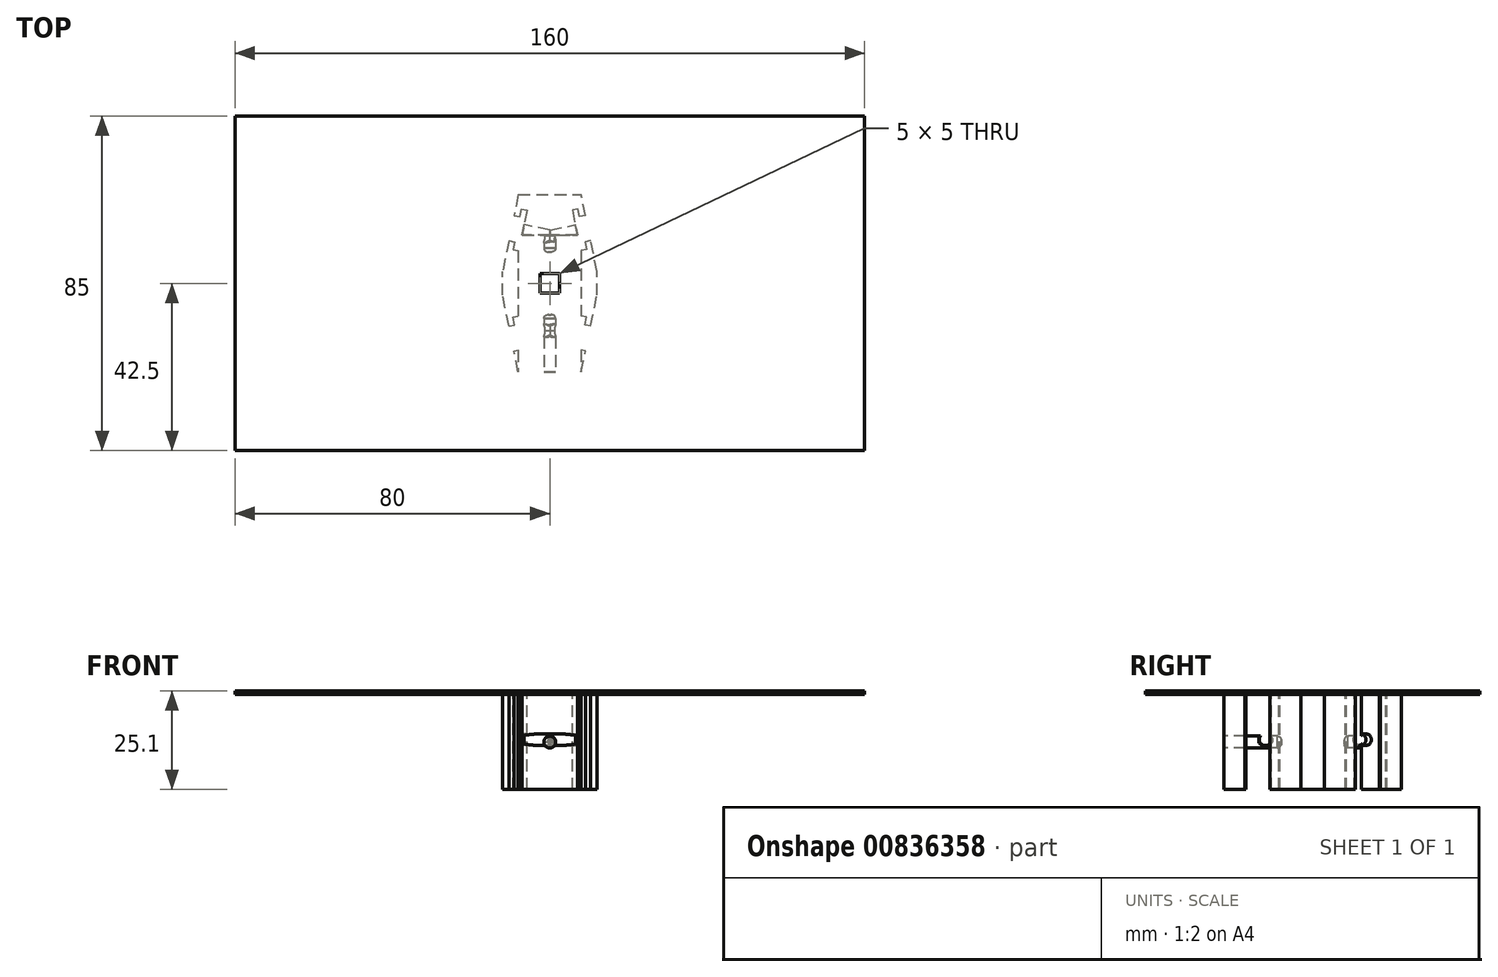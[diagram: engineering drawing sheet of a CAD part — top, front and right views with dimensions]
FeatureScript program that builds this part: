
annotation { "Feature Type Name" : "Feature", "Feature Type Description" : "" }
export const myFeature = defineFeature(function(context is Context, id is Id, definition is map)
    precondition{}
    {
        {
            var Q0;
            Q0=qCreatedBy(makeId("Top.planeOp"),FACE);
            var sketch = newSketch(context, id + "F0", { "sketchPlane" : qUnion([Q0])});
            skLineSegment(sketch, "E0.bottom", {"start": v(80, -42.5) * mm, "end": v(-80, -42.5) * mm});
            skLineSegment(sketch, "E0.top", {"start": v(80, 42.5) * mm, "end": v(-80, 42.5) * mm});
            skLineSegment(sketch, "E0.left", {"start": v(80, -42.5) * mm, "end": v(80, 42.5) * mm});
            skLineSegment(sketch, "E0.right", {"start": v(-80, -42.5) * mm, "end": v(-80, 42.5) * mm});
            skPoint(sketch, "E0.middle", {"position": v(0, 0) * mm});
            skCircle(sketch, "E1", {"center": v(0, 0) * mm, "radius": 8 * mm});
            skSolve(sketch);
        }
        {
            var Q0;
            Q0=makeQuery(id+"F0.imprint","IMPRINT",FACE,{"disambiguationData":[TD([[makeQuery(id+"F0.imprint","IMPRINT",EDGE,{"derivedFrom":sQuery(id+"F0.wireOp",EDGE,"E1")}),1.0]])]});
            var Q1;
            Q1=makeQuery(id+"F0.imprint","IMPRINT",FACE,{"disambiguationData":[TD([[makeQuery(id+"F0.imprint","IMPRINT",EDGE,{"derivedFrom":sQuery(id+"F0.wireOp",EDGE,"E0.bottom")}),-1.0]])]});
            extrude(context, id + "F1", {"entities" : qUnion([Q0, Q1]), "depth" : 1 * mm, "offsetDistance" : 25 * mm});
        }
        {
            var Q0;
            Q0=makeQuery(id+"F1.opExtrude","CAP_FACE",FACE,{"disambiguationData":[OSD([sQuery(id+"F0.wireOp",EDGE,"E0.bottom"),sQuery(id+"F0.wireOp",EDGE,"E0.top"),sQuery(id+"F0.wireOp",EDGE,"E0.left"),sQuery(id+"F0.wireOp",EDGE,"E0.right")])],"isStart":true});
            var sketch = newSketch(context, id + "F2", { "sketchPlane" : qUnion([Q0])});
            skCircle(sketch, "E2", {"center": v(0, 0) * mm, "radius": 8 * mm});
            skSolve(sketch);
        }
        {
            var Q0;
            Q0=makeQuery(id+"F1.opExtrude","CAP_FACE",FACE,{"disambiguationData":[OSD([sQuery(id+"F0.wireOp",EDGE,"E0.bottom"),sQuery(id+"F0.wireOp",EDGE,"E0.top"),sQuery(id+"F0.wireOp",EDGE,"E0.left"),sQuery(id+"F0.wireOp",EDGE,"E0.right")])],"isStart":true});
            var sketch = newSketch(context, id + "F3", { "sketchPlane" : qUnion([Q0])});
            skLineSegment(sketch, "E3", {"start": v(80, -42.5) * mm, "end": v(80, -3) * mm});
            skLineSegment(sketch, "E4", {"start": v(80, 42.5) * mm, "end": v(80, 3) * mm});
            skLineSegment(sketch, "E5", {"start": v(-80, 42.5) * mm, "end": v(-80, 3) * mm});
            skLineSegment(sketch, "E6", {"start": v(-80, -42.5) * mm, "end": v(-80, -3) * mm});
            skLineSegment(sketch, "E7", {"start": v(-80, 3) * mm, "end": v(-12, 3) * mm});
            skLineSegment(sketch, "E8", {"start": v(-80, -3) * mm, "end": v(-12, -3) * mm});
            skLineSegment(sketch, "E9", {"start": v(80, 3) * mm, "end": v(12, 3) * mm});
            skLineSegment(sketch, "E10", {"start": v(80, -3) * mm, "end": v(12, -3) * mm});
            skLineSegment(sketch, "E11", {"start": v(-12, 3) * mm, "end": v(-12, -3) * mm});
            skLineSegment(sketch, "E12", {"start": v(12, 3) * mm, "end": v(12, -3) * mm});
            skLineSegment(sketch, "E13", {"start": v(-80, -42.5) * mm, "end": v(-8, -42.5) * mm});
            skLineSegment(sketch, "E14", {"start": v(-80, -42.5) * mm, "end": v(8, -42.5) * mm});
            skLineSegment(sketch, "E15", {"start": v(-80, 42.5) * mm, "end": v(-8, 42.5) * mm});
            skLineSegment(sketch, "E16", {"start": v(-80, 42.5) * mm, "end": v(8, 42.5) * mm});
            skLineSegment(sketch, "E17", {"start": v(-8, 42.5) * mm, "end": v(-8, 22.5) * mm});
            skLineSegment(sketch, "E18", {"start": v(8, 42.5) * mm, "end": v(8, 22.5) * mm});
            skLineSegment(sketch, "E19", {"start": v(-8, -42.5) * mm, "end": v(-8, -22.5) * mm});
            skLineSegment(sketch, "E20", {"start": v(8, -42.5) * mm, "end": v(8, -22.5) * mm});
            skLineSegment(sketch, "E21", {"start": v(-8, -22.5) * mm, "end": v(8, -22.5) * mm});
            skLineSegment(sketch, "E22", {"start": v(-8, 22.5) * mm, "end": v(8, 22.5) * mm});
            skLineSegment(sketch, "E23", {"start": v(8, 22.5) * mm, "end": v(12, 3) * mm});
            skLineSegment(sketch, "E24", {"start": v(12, -3) * mm, "end": v(8, -22.5) * mm});
            skLineSegment(sketch, "E25", {"start": v(-8, -22.5) * mm, "end": v(-12, -3) * mm});
            skLineSegment(sketch, "E26", {"start": v(-8, 22.5) * mm, "end": v(-12, 3) * mm});
            skLineSegment(sketch, "E27", {"start": v(12, 3) * mm, "end": v(11.2, 6.92) * mm});
            skLineSegment(sketch, "E28", {"start": v(12, 3) * mm, "end": v(10.4, 10.84) * mm});
            skLineSegment(sketch, "E29", {"start": v(12, 3) * mm, "end": v(9.09, 17.2) * mm});
            skLineSegment(sketch, "E30", {"start": v(12, 3) * mm, "end": v(9.39, 15.73) * mm});
            skLineSegment(sketch, "E31", {"start": v(9.09, 17.2) * mm, "end": v(7.62, 16.9) * mm});
            skLineSegment(sketch, "E32", {"start": v(7.62, 16.9) * mm, "end": v(7.22, 18.86) * mm});
            skLineSegment(sketch, "E33", {"start": v(7.22, 18.86) * mm, "end": v(5.75, 18.56) * mm});
            skLineSegment(sketch, "E34", {"start": v(10.4, 10.84) * mm, "end": v(8.92, 10.54) * mm});
            skLineSegment(sketch, "E35", {"start": v(8.92, 10.54) * mm, "end": v(9.32, 8.58) * mm});
            skLineSegment(sketch, "E36", {"start": v(9.32, 8.58) * mm, "end": v(7.86, 8.27) * mm});
            skLineSegment(sketch, "E37", {"start": v(7.86, 8.27) * mm, "end": v(5.75, 18.56) * mm});
            skLineSegment(sketch, "E38", {"start": v(-12, 3) * mm, "end": v(-11.2, 6.92) * mm});
            skLineSegment(sketch, "E39", {"start": v(-12, 3) * mm, "end": v(-10.4, 10.84) * mm});
            skLineSegment(sketch, "E40", {"start": v(-12, 3) * mm, "end": v(-9.09, 17.2) * mm});
            skLineSegment(sketch, "E41", {"start": v(-12, 3) * mm, "end": v(-9.39, 15.73) * mm});
            skLineSegment(sketch, "E42", {"start": v(-10.4, 10.84) * mm, "end": v(-8.92, 10.54) * mm});
            skLineSegment(sketch, "E43", {"start": v(-8.92, 10.54) * mm, "end": v(-9.32, 8.58) * mm});
            skLineSegment(sketch, "E44", {"start": v(-9.32, 8.58) * mm, "end": v(-7.86, 8.27) * mm});
            skLineSegment(sketch, "E45", {"start": v(-9.09, 17.2) * mm, "end": v(-7.62, 16.9) * mm});
            skLineSegment(sketch, "E46", {"start": v(-7.62, 16.9) * mm, "end": v(-7.22, 18.86) * mm});
            skLineSegment(sketch, "E47", {"start": v(-7.22, 18.86) * mm, "end": v(-5.75, 18.56) * mm});
            skLineSegment(sketch, "E48", {"start": v(-5.75, 18.56) * mm, "end": v(-7.86, 8.27) * mm});
            skLineSegment(sketch, "E49", {"start": v(12, -3) * mm, "end": v(10.8, -8.88) * mm});
            skLineSegment(sketch, "E50", {"start": v(12, -3) * mm, "end": v(10.4, -10.84) * mm});
            skLineSegment(sketch, "E51", {"start": v(12, -3) * mm, "end": v(9.09, -17.2) * mm});
            skLineSegment(sketch, "E52", {"start": v(12, -3) * mm, "end": v(8.99, -17.7) * mm});
            skLineSegment(sketch, "E53", {"start": v(10.4, -10.84) * mm, "end": v(8.92, -10.54) * mm});
            skLineSegment(sketch, "E54", {"start": v(8.92, -10.54) * mm, "end": v(9.32, -8.58) * mm});
            skLineSegment(sketch, "E55", {"start": v(9.32, -8.58) * mm, "end": v(7.86, -8.27) * mm});
            skLineSegment(sketch, "E56", {"start": v(9.09, -17.2) * mm, "end": v(7.62, -16.9) * mm});
            skLineSegment(sketch, "E57", {"start": v(7.62, -16.9) * mm, "end": v(7.22, -18.86) * mm});
            skLineSegment(sketch, "E58", {"start": v(7.22, -18.86) * mm, "end": v(5.75, -18.56) * mm});
            skLineSegment(sketch, "E59", {"start": v(5.75, -18.56) * mm, "end": v(7.86, -8.27) * mm});
            skLineSegment(sketch, "E60", {"start": v(-12, -3) * mm, "end": v(-11.2, -6.92) * mm});
            skLineSegment(sketch, "E61", {"start": v(-12, -3) * mm, "end": v(-10.4, -10.84) * mm});
            skLineSegment(sketch, "E62", {"start": v(-12, -3) * mm, "end": v(-9.09, -17.2) * mm});
            skLineSegment(sketch, "E63", {"start": v(-12, -3) * mm, "end": v(-9.39, -15.73) * mm});
            skLineSegment(sketch, "E64", {"start": v(-10.4, -10.84) * mm, "end": v(-8.92, -10.54) * mm});
            skLineSegment(sketch, "E65", {"start": v(-8.92, -10.54) * mm, "end": v(-9.32, -8.58) * mm});
            skLineSegment(sketch, "E66", {"start": v(-9.32, -8.58) * mm, "end": v(-7.86, -8.27) * mm});
            skLineSegment(sketch, "E67", {"start": v(-9.09, -17.2) * mm, "end": v(-7.62, -16.9) * mm});
            skLineSegment(sketch, "E68", {"start": v(-7.62, -16.9) * mm, "end": v(-7.22, -18.86) * mm});
            skLineSegment(sketch, "E69", {"start": v(-7.22, -18.86) * mm, "end": v(-5.75, -18.56) * mm});
            skLineSegment(sketch, "E70", {"start": v(-5.75, -18.56) * mm, "end": v(-7.86, -8.27) * mm});
            skCircle(sketch, "E71", {"center": v(0, 0) * mm, "radius": 8 * mm});
            skLineSegment(sketch, "E72", {"start": v(9.09, 17.2) * mm, "end": v(10.4, 10.84) * mm});
            skLineSegment(sketch, "E73", {"start": v(10.4, -10.84) * mm, "end": v(9.09, -17.2) * mm});
            skLineSegment(sketch, "E74", {"start": v(-10.4, -10.84) * mm, "end": v(-9.09, -17.2) * mm});
            skSolve(sketch);
        }
        {
            var Q0;
            {var subQ5=sQuery(id+"F3.wireOp",EDGE,"E11");Q0=makeQuery(id+"F3.imprint","IMPRINT",FACE,{"disambiguationData":[TD([[makeQuery(id+"F3.imprint","IMPRINT",EDGE,{"derivedFrom":subQ5}),1.0]])]});}
            extrude(context, id + "F4", {"entities" : qUnion([Q0]), "operationType" : NewBodyOperationType.ADD, "depth" : 24.1 * mm, "offsetDistance" : 25 * mm});
        }
        {
            var Q0;
            Q0=makeQuery(id+"F4.opExtrude","SWEPT_FACE",FACE,{"disambiguationData":[OSD([sQuery(id+"F3.wireOp",EDGE,"E59")])]});
            var sketch = newSketch(context, id + "F5", { "sketchPlane" : qUnion([Q0])});
            skLineSegment(sketch, "E75", {"start": v(11.78, 0) * mm, "end": v(11.78, -11.45) * mm});
            skCircle(sketch, "E76", {"center": v(11.78, -11.45) * mm, "radius": 1.5 * mm});
            skSolve(sketch);
        }
        {
            var Q0;
            Q0=makeQuery(id+"F5.imprint","IMPRINT",FACE,{"disambiguationData":[TD([[makeQuery(id+"F5.imprint","IMPRINT",EDGE,{"derivedFrom":sQuery(id+"F5.wireOp",EDGE,"E76")}),1.0]])]});
            var Q1;
            Q1=sQuery(id+"F5.wireOp",EDGE,"E76");
            extrude(context, id + "F6", {"entities" : qUnion([Q0]), "operationType" : NewBodyOperationType.REMOVE, "surfaceEntities" : qUnion([Q1]), "oppositeDirection" : true, "depth" : 8.71 * mm, "offsetDistance" : 25 * mm});
        }
        {
            var Q0;
            Q0=makeQuery(id+"F4.opExtrude","SWEPT_FACE",FACE,{"disambiguationData":[OSD([sQuery(id+"F3.wireOp",EDGE,"E70")])]});
            var sketch = newSketch(context, id + "F7", { "sketchPlane" : qUnion([Q0])});
            skLineSegment(sketch, "E77", {"start": v(-11.78, 0) * mm, "end": v(-11.78, -11.45) * mm});
            skCircle(sketch, "E78", {"center": v(-11.78, -11.45) * mm, "radius": 1.5 * mm});
            skSolve(sketch);
        }
        {
            var Q0;
            Q0=makeQuery(id+"F7.imprint","IMPRINT",FACE,{"disambiguationData":[TD([[makeQuery(id+"F7.imprint","IMPRINT",EDGE,{"derivedFrom":sQuery(id+"F7.wireOp",EDGE,"E78")}),1.0]])]});
            var Q1;
            Q1=sQuery(id+"F7.wireOp",EDGE,"E78");
            extrude(context, id + "F8", {"entities" : qUnion([Q0]), "operationType" : NewBodyOperationType.REMOVE, "surfaceEntities" : qUnion([Q1]), "oppositeDirection" : true, "depth" : 8.18 * mm, "offsetDistance" : 25 * mm});
        }
        {
            var Q0;
            Q0=makeQuery(id+"F4.opExtrude","SWEPT_FACE",FACE,{"disambiguationData":[OSD([sQuery(id+"F3.wireOp",EDGE,"E48")])]});
            var sketch = newSketch(context, id + "F9", { "sketchPlane" : qUnion([Q0])});
            skLineSegment(sketch, "E79", {"start": v(11.78, 0) * mm, "end": v(11.78, -11.45) * mm});
            skCircle(sketch, "E80", {"center": v(11.78, -11.45) * mm, "radius": 1.5 * mm});
            skSolve(sketch);
        }
        {
            var Q0;
            Q0=qSketchRegion(id+"F9",true);
            extrude(context, id + "F10", {"entities" : qUnion([Q0]), "operationType" : NewBodyOperationType.REMOVE, "oppositeDirection" : true, "depth" : 8.71 * mm, "offsetDistance" : 25 * mm});
        }
        {
            var Q0;
            Q0=makeQuery(id+"F4.opExtrude","SWEPT_FACE",FACE,{"disambiguationData":[OSD([sQuery(id+"F3.wireOp",EDGE,"E37")])]});
            var sketch = newSketch(context, id + "F11", { "sketchPlane" : qUnion([Q0])});
            skLineSegment(sketch, "E81", {"start": v(-11.78, 0) * mm, "end": v(-11.78, -11.45) * mm});
            skCircle(sketch, "E82", {"center": v(-11.78, -11.45) * mm, "radius": 1.5 * mm});
            skSolve(sketch);
        }
        {
            var Q0;
            Q0=qSketchRegion(id+"F11",true);
            extrude(context, id + "F12", {"entities" : qUnion([Q0]), "operationType" : NewBodyOperationType.REMOVE, "oppositeDirection" : true, "depth" : 8.71 * mm, "offsetDistance" : 25 * mm});
        }
        {
            var Q0;
            Q0=makeQuery(id+"F4.boolean.opBoolean","SPLIT",FACE,{"disambiguationData":[TD([makeQuery(id+"F4.opExtrude","SWEPT_FACE",FACE,{"disambiguationData":[OSD([sQuery(id+"F3.wireOp",EDGE,"E71")])]})])],"derivedFrom":makeQuery(id+"F1.opExtrude","CAP_FACE",FACE,{"disambiguationData":[OSD([sQuery(id+"F0.wireOp",EDGE,"E0.bottom"),sQuery(id+"F0.wireOp",EDGE,"E0.top"),sQuery(id+"F0.wireOp",EDGE,"E0.left"),sQuery(id+"F0.wireOp",EDGE,"E0.right")])],"isStart":true})});
            var sketch = newSketch(context, id + "F13", { "sketchPlane" : qUnion([Q0])});
            skLineSegment(sketch, "E83.bottom", {"start": v(2.5, -2.5) * mm, "end": v(-2.5, -2.5) * mm});
            skLineSegment(sketch, "E83.top", {"start": v(2.5, 2.5) * mm, "end": v(-2.5, 2.5) * mm});
            skLineSegment(sketch, "E83.left", {"start": v(2.5, -2.5) * mm, "end": v(2.5, 2.5) * mm});
            skLineSegment(sketch, "E83.right", {"start": v(-2.5, -2.5) * mm, "end": v(-2.5, 2.5) * mm});
            skPoint(sketch, "E83.middle", {"position": v(0, 0) * mm});
            skSolve(sketch);
        }
        {
            var Q0;
            Q0=qSketchRegion(id+"F13",true);
            extrude(context, id + "F14", {"entities" : qUnion([Q0]), "operationType" : NewBodyOperationType.REMOVE, "oppositeDirection" : true, "depth" : 25 * mm, "offsetDistance" : 25 * mm});
        }
        {
            var Q0;
            Q0=makeQuery(id+"F4.opExtrude","SWEPT_FACE",FACE,{"disambiguationData":[OSD([sQuery(id+"F3.wireOp",EDGE,"E22")])]});
            var sketch = newSketch(context, id + "F15", { "sketchPlane" : qUnion([Q0])});
            skLineSegment(sketch, "E84", {"start": v(0, -24.1) * mm, "end": v(0, 0) * mm});
            skLineSegment(sketch, "E85", {"start": v(0, 0) * mm, "end": v(0, -12.05) * mm});
            skCircle(sketch, "E86", {"center": v(0, -12.05) * mm, "radius": 1.5 * mm});
            skSolve(sketch);
        }
        {
            var Q0;
            {var subQ0=sQuery(id+"F15.wireOp",EDGE,"E85");var subQ1=sQuery(id+"F15.wireOp",EDGE,"E84");var subQ2=makeQuery(id+"F15.imprint","INTERSECT",VERTEX,{"derivedFrom":[subQ1,subQ0]});Q0=makeQuery(id+"F15.imprint","IMPRINT",FACE,{"disambiguationData":[TD([[makeQuery(id+"F15.imprint","IMPRINT",EDGE,{"disambiguationData":[TD([[subQ2,1.0]])],"derivedFrom":subQ1}),1.0]])]});}
            var Q1;
            {var subQ0=sQuery(id+"F15.wireOp",EDGE,"E85");var subQ1=sQuery(id+"F15.wireOp",EDGE,"E84");var subQ2=makeQuery(id+"F15.imprint","INTERSECT",VERTEX,{"derivedFrom":[subQ1,subQ0]});Q1=makeQuery(id+"F15.imprint","IMPRINT",FACE,{"disambiguationData":[TD([[makeQuery(id+"F15.imprint","IMPRINT",EDGE,{"disambiguationData":[TD([[subQ2,1.0]])],"derivedFrom":subQ1}),-1.0]])]});}
            var Q2;
            Q2=sQuery(id+"F15.wireOp",EDGE,"E86");
            extrude(context, id + "F16", {"entities" : qUnion([Q0, Q1]), "operationType" : NewBodyOperationType.REMOVE, "surfaceEntities" : qUnion([Q2]), "oppositeDirection" : true, "depth" : 34.8 * mm, "offsetDistance" : 25 * mm});
        }
        {
            var Q0;
            Q0=makeQuery(id+"F16.boolean.opBoolean","INTERSECT",EDGE,{"disambiguationData":[OD(0.0)],"derivedFrom":[makeQuery(id+"F4.opExtrude","SWEPT_FACE",FACE,{"disambiguationData":[OSD([sQuery(id+"F3.wireOp",EDGE,"E71")])]}),makeQuery(id+"F16.opExtrude","SWEPT_FACE",FACE,{"disambiguationData":[OSD([sQuery(id+"F15.wireOp",EDGE,"E86")])]})]});
            fillet(context, id + "F17", {"entities" : qUnion([Q0]), "radius" : 1 * mm, "tangentPropagation" : true, "allowEdgeOverflow" : false});
        }
        {
            var Q0;
            Q0=makeQuery(id+"F16.boolean.opBoolean","INTERSECT",EDGE,{"disambiguationData":[OD(1.0)],"derivedFrom":[makeQuery(id+"F4.opExtrude","SWEPT_FACE",FACE,{"disambiguationData":[OSD([sQuery(id+"F3.wireOp",EDGE,"E71")])]}),makeQuery(id+"F16.opExtrude","SWEPT_FACE",FACE,{"disambiguationData":[OSD([sQuery(id+"F15.wireOp",EDGE,"E86")])]})]});
            fillet(context, id + "F18", {"entities" : qUnion([Q0]), "radius" : 1 * mm, "tangentPropagation" : true, "allowEdgeOverflow" : false});
        }
        {
            var Q0;
            Q0=makeQuery(id+"F4.opExtrude","SWEPT_FACE",FACE,{"disambiguationData":[OSD([sQuery(id+"F3.wireOp",EDGE,"E22")])]});
            var sketch = newSketch(context, id + "F19", { "sketchPlane" : qUnion([Q0])});
            skCircle(sketch, "E87", {"center": v(0, -12.05) * mm, "radius": 1.5 * mm});
            skSolve(sketch);
        }
        {
            var Q0;
            Q0=qSketchRegion(id+"F19",true);
            extrude(context, id + "F20", {"entities" : qUnion([Q0]), "operationType" : NewBodyOperationType.ADD, "oppositeDirection" : true, "depth" : 8.88 * mm, "offsetDistance" : 25 * mm});
        }
    });
